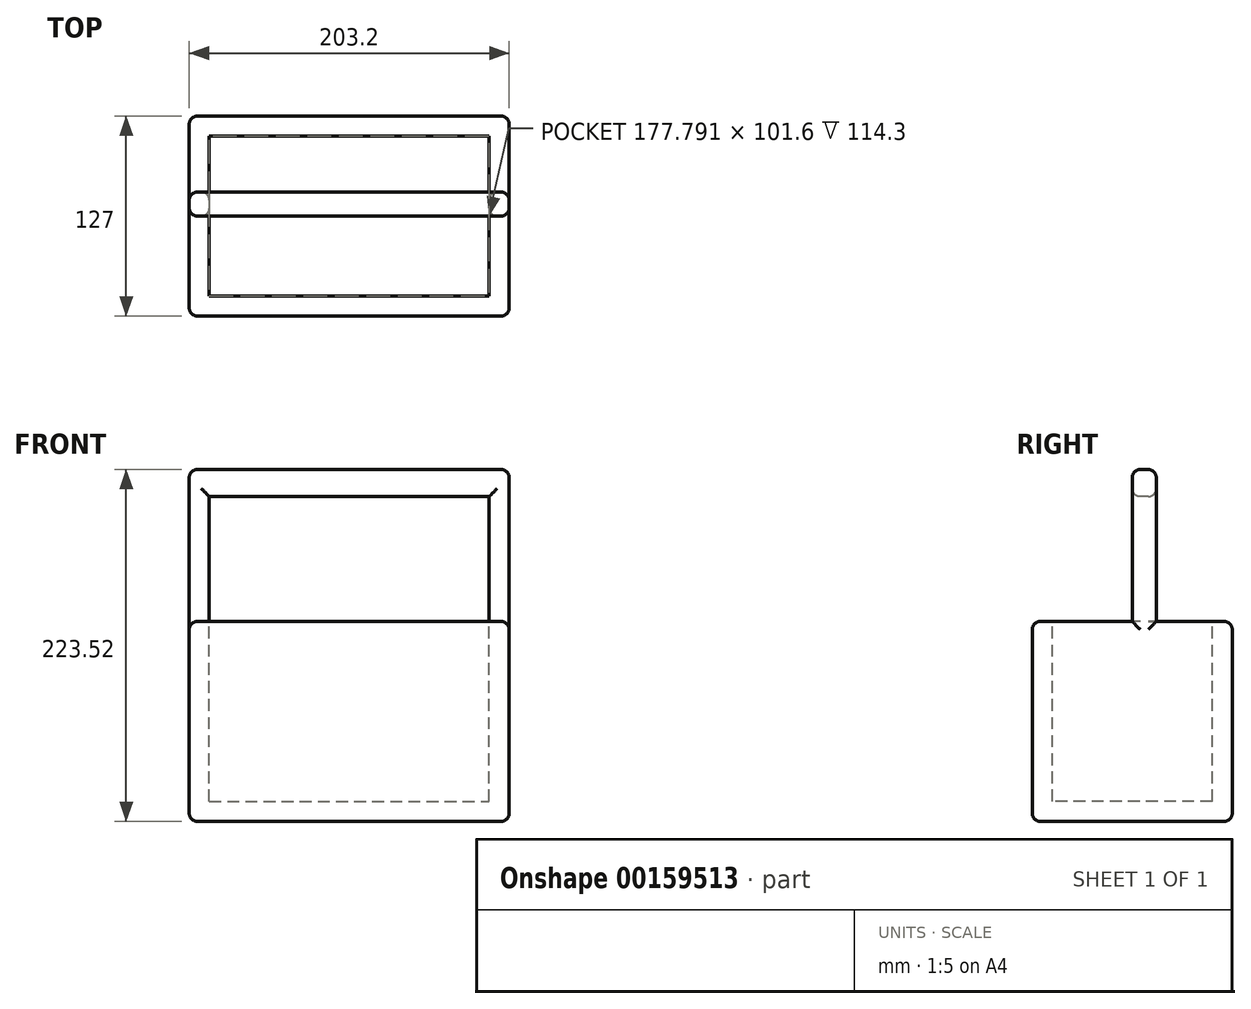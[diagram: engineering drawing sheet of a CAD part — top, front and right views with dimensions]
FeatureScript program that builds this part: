
annotation { "Feature Type Name" : "Feature", "Feature Type Description" : "" }
export const myFeature = defineFeature(function(context is Context, id is Id, definition is map)
    precondition{}
    {
        {
            var Q0;
            Q0=qCreatedBy(makeId("Top.planeOp"),FACE);
            var sketch = newSketch(context, id + "F0", { "sketchPlane" : qUnion([Q0])});
            skLineSegment(sketch, "E0.bottom", {"start": v(101.6, 63.5) * mm, "end": v(-101.6, 63.5) * mm});
            skLineSegment(sketch, "E0.top", {"start": v(101.6, -63.5) * mm, "end": v(-101.6, -63.5) * mm});
            skLineSegment(sketch, "E0.left", {"start": v(101.6, 63.5) * mm, "end": v(101.6, -63.5) * mm});
            skLineSegment(sketch, "E0.right", {"start": v(-101.6, 63.5) * mm, "end": v(-101.6, -63.5) * mm});
            skPoint(sketch, "E0.middle", {"position": v(0, 0) * mm});
            skSolve(sketch);
        }
        {
            var Q0;
            Q0 = qSketchRegion(id + "F0", true);
            extrude(context, id + "F1", {"entities" : qUnion([Q0]), "depth" : 127 * mm});
        }
        {
            var Q0;
            Q0=makeQuery(id+"F1.opExtrude","CAP_FACE",FACE,{"disambiguationData":[OSD([sQuery(id+"F0.wireOp",EDGE,"E0.bottom"),sQuery(id+"F0.wireOp",EDGE,"E0.top"),sQuery(id+"F0.wireOp",EDGE,"E0.left"),sQuery(id+"F0.wireOp",EDGE,"E0.right")])],"isStart":false});
            var sketch = newSketch(context, id + "F2", { "sketchPlane" : qUnion([Q0])});
            skLineSegment(sketch, "E1.bottom", {"start": v(-88.9, 50.8) * mm, "end": v(88.9, 50.8) * mm});
            skLineSegment(sketch, "E1.top", {"start": v(-88.9, -50.8) * mm, "end": v(88.9, -50.8) * mm});
            skLineSegment(sketch, "E1.left", {"start": v(-88.9, 50.8) * mm, "end": v(-88.9, -50.8) * mm});
            skLineSegment(sketch, "E1.right", {"start": v(88.9, 50.8) * mm, "end": v(88.9, -50.8) * mm});
            skSolve(sketch);
        }
        {
            var Q0;
            Q0=makeQuery(id+"F2.imprint","IMPRINT",FACE,{"disambiguationData":[TD([[makeQuery(id+"F2.imprint","IMPRINT",EDGE,{"derivedFrom":sQuery(id+"F2.wireOp",EDGE,"E1.bottom")}),-1.0]])]});
            extrude(context, id + "F3", {"entities" : qUnion([Q0]), "operationType" : NewBodyOperationType.REMOVE, "oppositeDirection" : true, "depth" : 114.3 * mm});
        }
        {
            var Q0;
            Q0=makeQuery(id+"F1.opExtrude","CAP_FACE",FACE,{"disambiguationData":[OSD([sQuery(id+"F0.wireOp",EDGE,"E0.bottom"),sQuery(id+"F0.wireOp",EDGE,"E0.top"),sQuery(id+"F0.wireOp",EDGE,"E0.left"),sQuery(id+"F0.wireOp",EDGE,"E0.right")])],"isStart":false});
            var sketch = newSketch(context, id + "F4", { "sketchPlane" : qUnion([Q0])});
            skLineSegment(sketch, "E2.bottom", {"start": v(-101.6, 15.24) * mm, "end": v(-88.9, 15.24) * mm});
            skLineSegment(sketch, "E2.top", {"start": v(-101.6, 0) * mm, "end": v(-88.9, 0) * mm});
            skLineSegment(sketch, "E2.left", {"start": v(-101.6, 15.24) * mm, "end": v(-101.6, 0) * mm});
            skLineSegment(sketch, "E2.right", {"start": v(-88.9, 15.24) * mm, "end": v(-88.9, 0) * mm});
            skLineSegment(sketch, "E3.bottom", {"start": v(88.9, 0) * mm, "end": v(101.6, 0) * mm});
            skLineSegment(sketch, "E3.top", {"start": v(88.9, 15.24) * mm, "end": v(101.6, 15.24) * mm});
            skLineSegment(sketch, "E3.left", {"start": v(88.9, 0) * mm, "end": v(88.9, 15.24) * mm});
            skLineSegment(sketch, "E3.right", {"start": v(101.6, 0) * mm, "end": v(101.6, 15.24) * mm});
            skSolve(sketch);
        }
        {
            var Q0;
            Q0 = qSketchRegion(id + "F4", true);
            extrude(context, id + "F5", {"entities" : qUnion([Q0]), "operationType" : NewBodyOperationType.ADD, "depth" : 96.52 * mm});
        }
        {
            var Q0;
            Q0=makeQuery(id+"F5.boolean.opBoolean","MERGE",FACE,{"derivedFrom":[makeQuery(id+"F3.boolean.opBoolean","COPY",FACE,{"derivedFrom":makeQuery(id+"F3.opExtrude","SWEPT_FACE",FACE,{"disambiguationData":[OSD([sQuery(id+"F2.wireOp",EDGE,"E1.left")])]})}),makeQuery(id+"F5.opExtrude","SWEPT_FACE",FACE,{"disambiguationData":[OSD([sQuery(id+"F4.wireOp",EDGE,"E2.right")])]})]});
            var sketch = newSketch(context, id + "F6", { "sketchPlane" : qUnion([Q0])});
            skLineSegment(sketch, "E4.bottom", {"start": v(15.24, 223.52) * mm, "end": v(0, 223.52) * mm});
            skLineSegment(sketch, "E4.top", {"start": v(15.24, 206.35) * mm, "end": v(0, 206.35) * mm});
            skLineSegment(sketch, "E4.left", {"start": v(15.24, 223.52) * mm, "end": v(15.24, 206.35) * mm});
            skLineSegment(sketch, "E4.right", {"start": v(0, 223.52) * mm, "end": v(0, 206.35) * mm});
            skSolve(sketch);
        }
        {
            var Q0;
            Q0 = qSketchRegion(id + "F6", true);
            extrude(context, id + "F7", {"entities" : qUnion([Q0]), "operationType" : NewBodyOperationType.ADD, "depth" : 177.8 * mm});
        }
        {
            var Q0;
            Q0=makeQuery(id+"F1.opExtrude","CAP_EDGE",EDGE,{"disambiguationData":[OSD([sQuery(id+"F0.wireOp",EDGE,"E0.top")])],"isStart":false});
            var Q1;
            Q1=makeQuery(id+"F7.boolean.opBoolean","MERGE",EDGE,{"derivedFrom":[makeQuery(id+"F5.opExtrude","CAP_EDGE",EDGE,{"disambiguationData":[OSD([sQuery(id+"F4.wireOp",EDGE,"E2.top")])],"isStart":false}),makeQuery(id+"F5.opExtrude","CAP_EDGE",EDGE,{"disambiguationData":[OSD([sQuery(id+"F4.wireOp",EDGE,"E3.bottom")])],"isStart":false}),makeQuery(id+"F7.opExtrude","SWEPT_EDGE",EDGE,{"disambiguationData":[OSD([sQuery(id+"F6.wireOp",EDGE,"E4.bottom"),sQuery(id+"F6.wireOp",EDGE,"E4.right")])]})]});
            var Q2;
            Q2=makeQuery(id+"F7.opExtrude","SWEPT_EDGE",EDGE,{"disambiguationData":[OSD([sQuery(id+"F2.wireOp",EDGE,"E1.left"),sQuery(id+"F4.wireOp",EDGE,"E2.top"),sQuery(id+"F4.wireOp",EDGE,"E2.right"),sQuery(id+"F6.wireOp",EDGE,"E4.top"),sQuery(id+"F6.wireOp",EDGE,"E4.right")])]});
            var Q3;
            Q3=makeQuery(id+"F5.opExtrude","SWEPT_EDGE",EDGE,{"disambiguationData":[OSD([sQuery(id+"F2.wireOp",EDGE,"E1.left"),sQuery(id+"F4.wireOp",EDGE,"E2.top"),sQuery(id+"F4.wireOp",EDGE,"E2.right")])]});
            var Q4;
            Q4=makeQuery(id+"F7.boolean.opBoolean","MERGE",EDGE,{"derivedFrom":[makeQuery(id+"F5.opExtrude","CAP_EDGE",EDGE,{"disambiguationData":[OSD([sQuery(id+"F4.wireOp",EDGE,"E2.bottom")])],"isStart":false}),makeQuery(id+"F5.opExtrude","CAP_EDGE",EDGE,{"disambiguationData":[OSD([sQuery(id+"F4.wireOp",EDGE,"E3.top")])],"isStart":false}),makeQuery(id+"F7.opExtrude","SWEPT_EDGE",EDGE,{"disambiguationData":[OSD([sQuery(id+"F6.wireOp",EDGE,"E4.bottom"),sQuery(id+"F6.wireOp",EDGE,"E4.left")])]})]});
            var Q5;
            Q5=makeQuery(id+"F5.opExtrude","SWEPT_EDGE",EDGE,{"disambiguationData":[OSD([sQuery(id+"F0.wireOp",EDGE,"E0.right"),sQuery(id+"F4.wireOp",EDGE,"E2.top"),sQuery(id+"F4.wireOp",EDGE,"E2.left")])]});
            var Q6;
            {var subQ0=sQuery(id+"F2.wireOp",EDGE,"E1.left");Q6=makeQuery(id+"F5.boolean.opBoolean","SPLIT",EDGE,{"disambiguationData":[TD([makeQuery(id+"F3.boolean.opBoolean","COPY",FACE,{"derivedFrom":makeQuery(id+"F3.opExtrude","SWEPT_FACE",FACE,{"disambiguationData":[OSD([sQuery(id+"F2.wireOp",EDGE,"E1.top")])]})})])],"derivedFrom":makeQuery(id+"F3.boolean.opBoolean","COPY",EDGE,{"derivedFrom":makeQuery(id+"F3.opExtrude","CAP_EDGE",EDGE,{"disambiguationData":[OSD([subQ0])],"isStart":true})})});}
            var Q7;
            Q7=makeQuery(id+"F3.boolean.opBoolean","COPY",EDGE,{"derivedFrom":makeQuery(id+"F3.opExtrude","CAP_EDGE",EDGE,{"disambiguationData":[OSD([sQuery(id+"F2.wireOp",EDGE,"E1.top")])],"isStart":true})});
            var Q8;
            {var subQ0=sQuery(id+"F2.wireOp",EDGE,"E1.right");Q8=makeQuery(id+"F5.boolean.opBoolean","SPLIT",EDGE,{"disambiguationData":[TD([makeQuery(id+"F3.boolean.opBoolean","COPY",FACE,{"derivedFrom":makeQuery(id+"F3.opExtrude","SWEPT_FACE",FACE,{"disambiguationData":[OSD([sQuery(id+"F2.wireOp",EDGE,"E1.top")])]})})])],"derivedFrom":makeQuery(id+"F3.boolean.opBoolean","COPY",EDGE,{"derivedFrom":makeQuery(id+"F3.opExtrude","CAP_EDGE",EDGE,{"disambiguationData":[OSD([subQ0])],"isStart":true})})});}
            var Q9;
            {var subQ0=sQuery(id+"F0.wireOp",EDGE,"E0.right");var subQ1=sQuery(id+"F0.wireOp",EDGE,"E0.top");Q9=makeQuery(id+"F5.boolean.opBoolean","SPLIT",EDGE,{"disambiguationData":[TD([makeQuery(id+"F1.opExtrude","SWEPT_FACE",FACE,{"disambiguationData":[OSD([subQ1])]})])],"derivedFrom":makeQuery(id+"F1.opExtrude","CAP_EDGE",EDGE,{"disambiguationData":[OSD([subQ0])],"isStart":false})});}
            var Q10;
            {var subQ0=sQuery(id+"F0.wireOp",EDGE,"E0.left");var subQ1=sQuery(id+"F0.wireOp",EDGE,"E0.top");Q10=makeQuery(id+"F5.boolean.opBoolean","SPLIT",EDGE,{"disambiguationData":[TD([makeQuery(id+"F1.opExtrude","SWEPT_FACE",FACE,{"disambiguationData":[OSD([subQ1])]})])],"derivedFrom":makeQuery(id+"F1.opExtrude","CAP_EDGE",EDGE,{"disambiguationData":[OSD([subQ0])],"isStart":false})});}
            var Q11;
            Q11=makeQuery(id+"F1.opExtrude","SWEPT_EDGE",EDGE,{"disambiguationData":[OSD([sQuery(id+"F0.wireOp",EDGE,"E0.top"),sQuery(id+"F0.wireOp",EDGE,"E0.left")])]});
            var Q12;
            Q12=makeQuery(id+"F1.opExtrude","SWEPT_EDGE",EDGE,{"disambiguationData":[OSD([sQuery(id+"F0.wireOp",EDGE,"E0.top"),sQuery(id+"F0.wireOp",EDGE,"E0.right")])]});
            var Q13;
            Q13=makeQuery(id+"F5.opExtrude","SWEPT_EDGE",EDGE,{"disambiguationData":[OSD([sQuery(id+"F2.wireOp",EDGE,"E1.right"),sQuery(id+"F4.wireOp",EDGE,"E3.bottom"),sQuery(id+"F4.wireOp",EDGE,"E3.left")])]});
            var Q14;
            Q14=makeQuery(id+"F1.opExtrude","CAP_EDGE",EDGE,{"disambiguationData":[OSD([sQuery(id+"F0.wireOp",EDGE,"E0.top")])],"isStart":true});
            fillet(context, id + "F8", {"entities" : qUnion([Q0, Q1, Q2, Q3, Q4, Q5, Q6, Q7, Q8, Q9, Q10, Q11, Q12, Q13, Q14]), "radius" : 5.08 * mm, "tangentPropagation" : true, "allowEdgeOverflow" : false});
        }
        {
            var Q0;
            Q0=makeQuery(id+"F7.opExtrude","SWEPT_EDGE",EDGE,{"disambiguationData":[OSD([sQuery(id+"F2.wireOp",EDGE,"E1.left"),sQuery(id+"F4.wireOp",EDGE,"E2.bottom"),sQuery(id+"F4.wireOp",EDGE,"E2.right"),sQuery(id+"F6.wireOp",EDGE,"E4.top"),sQuery(id+"F6.wireOp",EDGE,"E4.left")])]});
            var Q1;
            Q1=makeQuery(id+"F5.opExtrude","SWEPT_EDGE",EDGE,{"disambiguationData":[OSD([sQuery(id+"F0.wireOp",EDGE,"E0.left"),sQuery(id+"F4.wireOp",EDGE,"E3.top"),sQuery(id+"F4.wireOp",EDGE,"E3.right")])]});
            var Q2;
            Q2=makeQuery(id+"F5.opExtrude","SWEPT_EDGE",EDGE,{"disambiguationData":[OSD([sQuery(id+"F2.wireOp",EDGE,"E1.right"),sQuery(id+"F4.wireOp",EDGE,"E3.top"),sQuery(id+"F4.wireOp",EDGE,"E3.left")])]});
            var Q3;
            Q3=makeQuery(id+"F5.opExtrude","SWEPT_EDGE",EDGE,{"disambiguationData":[OSD([sQuery(id+"F2.wireOp",EDGE,"E1.left"),sQuery(id+"F4.wireOp",EDGE,"E2.bottom"),sQuery(id+"F4.wireOp",EDGE,"E2.right")])]});
            var Q4;
            Q4=makeQuery(id+"F5.opExtrude","SWEPT_EDGE",EDGE,{"disambiguationData":[OSD([sQuery(id+"F0.wireOp",EDGE,"E0.right"),sQuery(id+"F4.wireOp",EDGE,"E2.bottom"),sQuery(id+"F4.wireOp",EDGE,"E2.left")])]});
            var Q5;
            Q5=makeQuery(id+"F1.opExtrude","CAP_EDGE",EDGE,{"disambiguationData":[OSD([sQuery(id+"F0.wireOp",EDGE,"E0.bottom")])],"isStart":false});
            var Q6;
            Q6=makeQuery(id+"F1.opExtrude","SWEPT_EDGE",EDGE,{"disambiguationData":[OSD([sQuery(id+"F0.wireOp",EDGE,"E0.bottom"),sQuery(id+"F0.wireOp",EDGE,"E0.right")])]});
            var Q7;
            Q7=makeQuery(id+"F1.opExtrude","SWEPT_FACE",FACE,{"disambiguationData":[OSD([sQuery(id+"F0.wireOp",EDGE,"E0.bottom")])]});
            var Q8;
            {var subQ0=sQuery(id+"F2.wireOp",EDGE,"E1.left");Q8=makeQuery(id+"F5.boolean.opBoolean","SPLIT",EDGE,{"disambiguationData":[TD([makeQuery(id+"F3.boolean.opBoolean","COPY",FACE,{"derivedFrom":makeQuery(id+"F3.opExtrude","SWEPT_FACE",FACE,{"disambiguationData":[OSD([sQuery(id+"F2.wireOp",EDGE,"E1.bottom")])]})})])],"derivedFrom":makeQuery(id+"F3.boolean.opBoolean","COPY",EDGE,{"derivedFrom":makeQuery(id+"F3.opExtrude","CAP_EDGE",EDGE,{"disambiguationData":[OSD([subQ0])],"isStart":true})})});}
            var Q9;
            Q9=makeQuery(id+"F3.boolean.opBoolean","COPY",EDGE,{"derivedFrom":makeQuery(id+"F3.opExtrude","CAP_EDGE",EDGE,{"disambiguationData":[OSD([sQuery(id+"F2.wireOp",EDGE,"E1.bottom")])],"isStart":true})});
            var Q10;
            {var subQ0=sQuery(id+"F2.wireOp",EDGE,"E1.right");Q10=makeQuery(id+"F5.boolean.opBoolean","SPLIT",EDGE,{"disambiguationData":[TD([makeQuery(id+"F3.boolean.opBoolean","COPY",FACE,{"derivedFrom":makeQuery(id+"F3.opExtrude","SWEPT_FACE",FACE,{"disambiguationData":[OSD([sQuery(id+"F2.wireOp",EDGE,"E1.bottom")])]})})])],"derivedFrom":makeQuery(id+"F3.boolean.opBoolean","COPY",EDGE,{"derivedFrom":makeQuery(id+"F3.opExtrude","CAP_EDGE",EDGE,{"disambiguationData":[OSD([subQ0])],"isStart":true})})});}
            var Q11;
            {var subQ0=sQuery(id+"F0.wireOp",EDGE,"E0.right");var subQ1=sQuery(id+"F0.wireOp",EDGE,"E0.bottom");Q11=makeQuery(id+"F5.boolean.opBoolean","SPLIT",EDGE,{"disambiguationData":[TD([makeQuery(id+"F1.opExtrude","SWEPT_FACE",FACE,{"disambiguationData":[OSD([subQ1])]})])],"derivedFrom":makeQuery(id+"F1.opExtrude","CAP_EDGE",EDGE,{"disambiguationData":[OSD([subQ0])],"isStart":false})});}
            var Q12;
            {var subQ0=sQuery(id+"F0.wireOp",EDGE,"E0.left");var subQ1=sQuery(id+"F0.wireOp",EDGE,"E0.bottom");Q12=makeQuery(id+"F5.boolean.opBoolean","SPLIT",EDGE,{"disambiguationData":[TD([makeQuery(id+"F1.opExtrude","SWEPT_FACE",FACE,{"disambiguationData":[OSD([subQ1])]})])],"derivedFrom":makeQuery(id+"F1.opExtrude","CAP_EDGE",EDGE,{"disambiguationData":[OSD([subQ0])],"isStart":false})});}
            var Q13;
            Q13=makeQuery(id+"F1.opExtrude","CAP_EDGE",EDGE,{"disambiguationData":[OSD([sQuery(id+"F0.wireOp",EDGE,"E0.left")])],"isStart":true});
            var Q14;
            Q14=makeQuery(id+"F1.opExtrude","CAP_EDGE",EDGE,{"disambiguationData":[OSD([sQuery(id+"F0.wireOp",EDGE,"E0.right")])],"isStart":true});
            fillet(context, id + "F9", {"entities" : qUnion([Q0, Q1, Q2, Q3, Q4, Q5, Q6, Q7, Q8, Q9, Q10, Q11, Q12, Q13, Q14]), "radius" : 5.08 * mm, "tangentPropagation" : true, "allowEdgeOverflow" : false});
        }
    });
